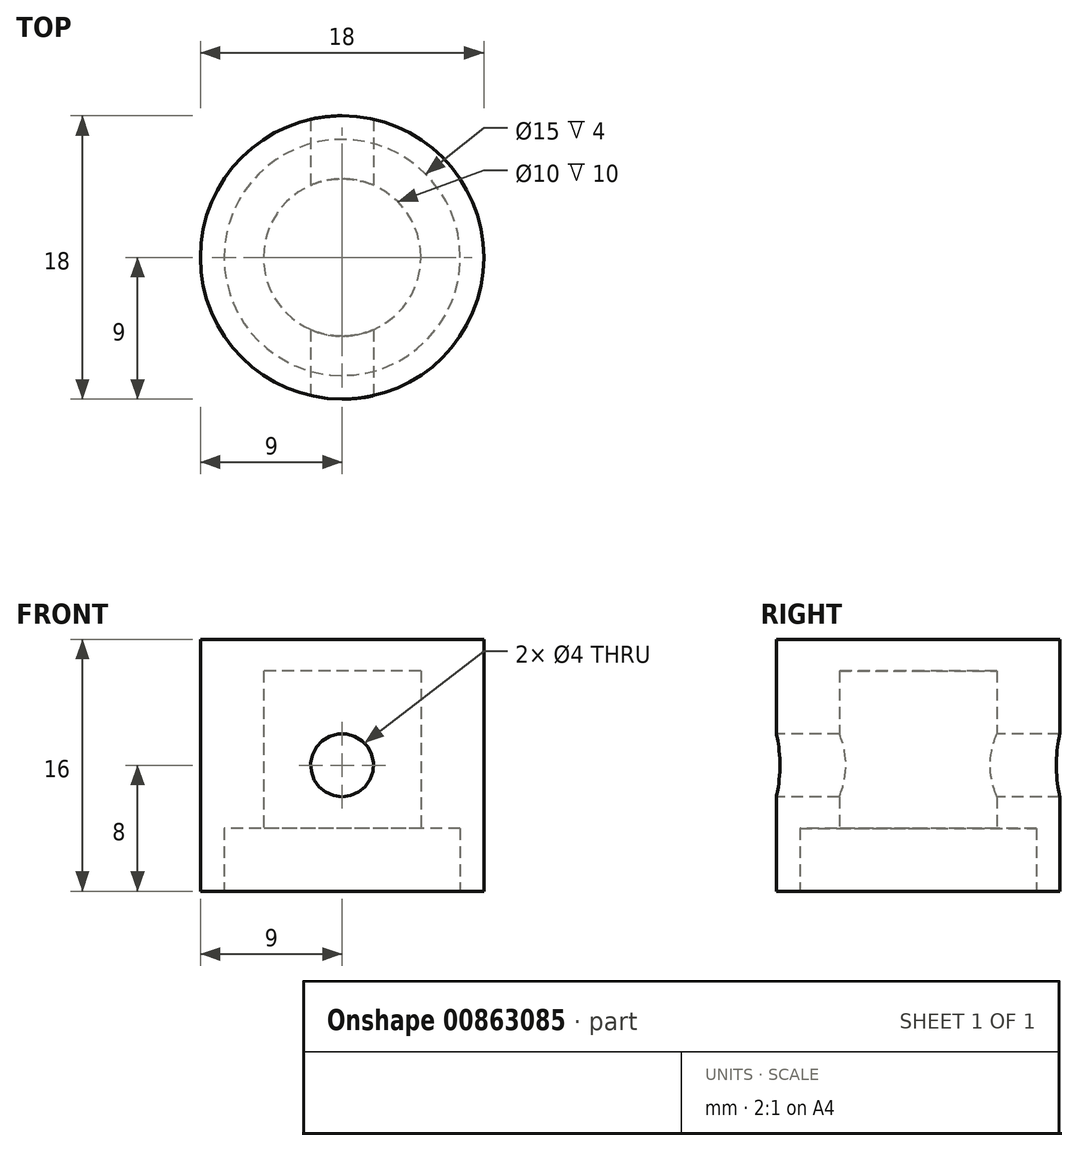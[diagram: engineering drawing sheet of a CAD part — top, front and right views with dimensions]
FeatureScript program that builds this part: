
annotation { "Feature Type Name" : "Feature", "Feature Type Description" : "" }
export const myFeature = defineFeature(function(context is Context, id is Id, definition is map)
    precondition{}
    {
        {
            var Q0;
            Q0=qCreatedBy(makeId("Top.planeOp"),FACE);
            var sketch = newSketch(context, id + "F0", { "sketchPlane" : qUnion([Q0])});
            skCircle(sketch, "E0", {"center": v(0, 0) * mm, "radius": 9 * mm});
            skCircle(sketch, "E1", {"center": v(0, 0) * mm, "radius": 7.5 * mm});
            skCircle(sketch, "E2", {"center": v(0, 0) * mm, "radius": 5 * mm});
            skSolve(sketch);
        }
        {
            var Q0;
            Q0 = qSketchRegion(id + "F0", true);
            var Q1;
            Q1=makeQuery(id+"F0.imprint","IMPRINT",FACE,{"disambiguationData":[TD([[makeQuery(id+"F0.imprint","IMPRINT",EDGE,{"derivedFrom":sQuery(id+"F0.wireOp",EDGE,"E1")}),1.0]])]});
            var Q2;
            Q2=makeQuery(id+"F0.imprint","IMPRINT",FACE,{"disambiguationData":[TD([[makeQuery(id+"F0.imprint","IMPRINT",EDGE,{"derivedFrom":sQuery(id+"F0.wireOp",EDGE,"E2")}),1.0]])]});
            extrude(context, id + "F1", {"entities" : qUnion([Q0, Q1, Q2]), "depth" : 16 * mm, "offsetDistance" : 25 * mm});
        }
        {
            var Q0;
            Q0=makeQuery(id+"F0.imprint","IMPRINT",FACE,{"disambiguationData":[TD([[makeQuery(id+"F0.imprint","IMPRINT",EDGE,{"derivedFrom":sQuery(id+"F0.wireOp",EDGE,"E2")}),1.0]])]});
            extrude(context, id + "F2", {"entities" : qUnion([Q0]), "operationType" : NewBodyOperationType.REMOVE, "depth" : 14 * mm, "offsetDistance" : 25 * mm});
        }
        {
            var Q0;
            Q0=makeQuery(id+"F0.imprint","IMPRINT",FACE,{"disambiguationData":[TD([[makeQuery(id+"F0.imprint","IMPRINT",EDGE,{"derivedFrom":sQuery(id+"F0.wireOp",EDGE,"E1")}),1.0]])]});
            extrude(context, id + "F3", {"entities" : qUnion([Q0]), "operationType" : NewBodyOperationType.REMOVE, "depth" : 4 * mm, "offsetDistance" : 25 * mm});
        }
        {
            var Q0;
            Q0=qCreatedBy(makeId("Front.planeOp"),FACE);
            var sketch = newSketch(context, id + "F4", { "sketchPlane" : qUnion([Q0])});
            skCircle(sketch, "E3", {"center": v(0, 8) * mm, "radius": 2 * mm});
            skSolve(sketch);
        }
        {
            var Q0;
            Q0 = qSketchRegion(id + "F4", true);
            extrude(context, id + "F5", {"entities" : qUnion([Q0]), "operationType" : NewBodyOperationType.REMOVE, "endBound" : BoundingType.SYMMETRIC, "oppositeDirection" : true, "depth" : 25 * mm, "offsetDistance" : 25 * mm});
        }
    });
